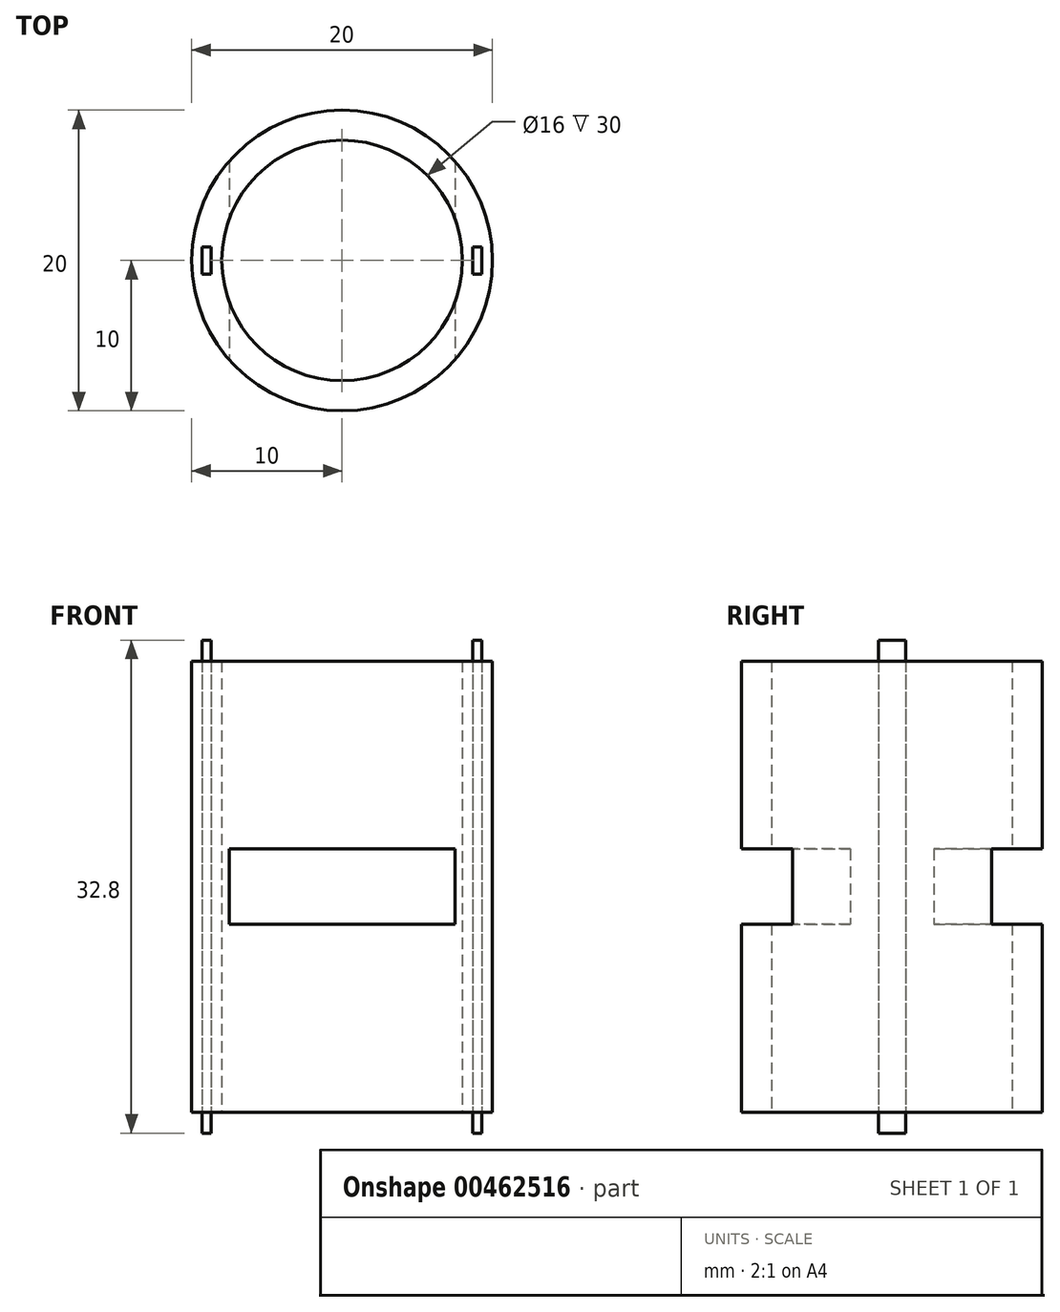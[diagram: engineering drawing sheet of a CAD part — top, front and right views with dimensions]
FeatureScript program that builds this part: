
annotation { "Feature Type Name" : "Feature", "Feature Type Description" : "" }
export const myFeature = defineFeature(function(context is Context, id is Id, definition is map)
    precondition{}
    {
        {
            var Q0;
            Q0=qCreatedBy(makeId("Top.planeOp"),FACE);
            var sketch = newSketch(context, id + "F0", { "sketchPlane" : qUnion([Q0])});
            skCircle(sketch, "E0", {"center": v(0, 0) * mm, "radius": 10 * mm});
            skCircle(sketch, "E1", {"center": v(0, 0) * mm, "radius": 8 * mm});
            skLineSegment(sketch, "E2.bottom", {"start": v(-9.3, -0.9) * mm, "end": v(-8.7, -0.9) * mm});
            skLineSegment(sketch, "E2.top", {"start": v(-9.3, 0.9) * mm, "end": v(-8.7, 0.9) * mm});
            skLineSegment(sketch, "E2.left", {"start": v(-9.3, -0.9) * mm, "end": v(-9.3, 0.9) * mm});
            skLineSegment(sketch, "E2.right", {"start": v(-8.7, -0.9) * mm, "end": v(-8.7, 0.9) * mm});
            skLineSegment(sketch, "E3.bottom", {"start": v(8.7, -0.9) * mm, "end": v(9.3, -0.9) * mm});
            skLineSegment(sketch, "E3.top", {"start": v(8.7, 0.9) * mm, "end": v(9.3, 0.9) * mm});
            skLineSegment(sketch, "E3.left", {"start": v(8.7, -0.9) * mm, "end": v(8.7, 0.9) * mm});
            skLineSegment(sketch, "E3.right", {"start": v(9.3, -0.9) * mm, "end": v(9.3, 0.9) * mm});
            skSolve(sketch);
        }
        {
            var Q0;
            Q0=makeQuery(id+"F0.imprint","IMPRINT",FACE,{"disambiguationData":[TD([[makeQuery(id+"F0.imprint","IMPRINT",EDGE,{"derivedFrom":sQuery(id+"F0.wireOp",EDGE,"E2.bottom")}),1.0]])]});
            var Q1;
            Q1=makeQuery(id+"F0.imprint","IMPRINT",FACE,{"disambiguationData":[TD([[makeQuery(id+"F0.imprint","IMPRINT",EDGE,{"derivedFrom":sQuery(id+"F0.wireOp",EDGE,"E3.bottom")}),1.0]])]});
            extrude(context, id + "F1", {"entities" : qUnion([Q0, Q1]), "depth" : 16.4 * mm, "hasSecondDirection" : true, "secondDirectionOppositeDirection" : true, "secondDirectionDepth" : 16.4 * mm});
        }
        {
            var Q0;
            Q0=qSketchRegion(id+"F0",true);
            extrude(context, id + "F2", {"entities" : qUnion([Q0]), "depth" : 15 * mm, "hasSecondDirection" : true, "secondDirectionOppositeDirection" : true, "secondDirectionDepth" : 15 * mm});
        }
        {
            var Q0;
            Q0=qCreatedBy(makeId("Front.planeOp"),FACE);
            var sketch = newSketch(context, id + "F3", { "sketchPlane" : qUnion([Q0])});
            skLineSegment(sketch, "E4.bottom", {"start": v(-7.5, 2.5) * mm, "end": v(7.5, 2.5) * mm});
            skLineSegment(sketch, "E4.top", {"start": v(-7.5, -2.5) * mm, "end": v(7.5, -2.5) * mm});
            skLineSegment(sketch, "E4.left", {"start": v(-7.5, 2.5) * mm, "end": v(-7.5, -2.5) * mm});
            skLineSegment(sketch, "E4.right", {"start": v(7.5, 2.5) * mm, "end": v(7.5, -2.5) * mm});
            skSolve(sketch);
        }
        {
            var Q0;
            Q0=qSketchRegion(id+"F3",true);
            extrude(context, id + "F4", {"entities" : qUnion([Q0]), "operationType" : NewBodyOperationType.REMOVE, "oppositeDirection" : true, "depth" : 20 * mm, "hasSecondDirection" : true, "secondDirectionOppositeDirection" : false, "secondDirectionDepth" : 20 * mm});
        }
    });
